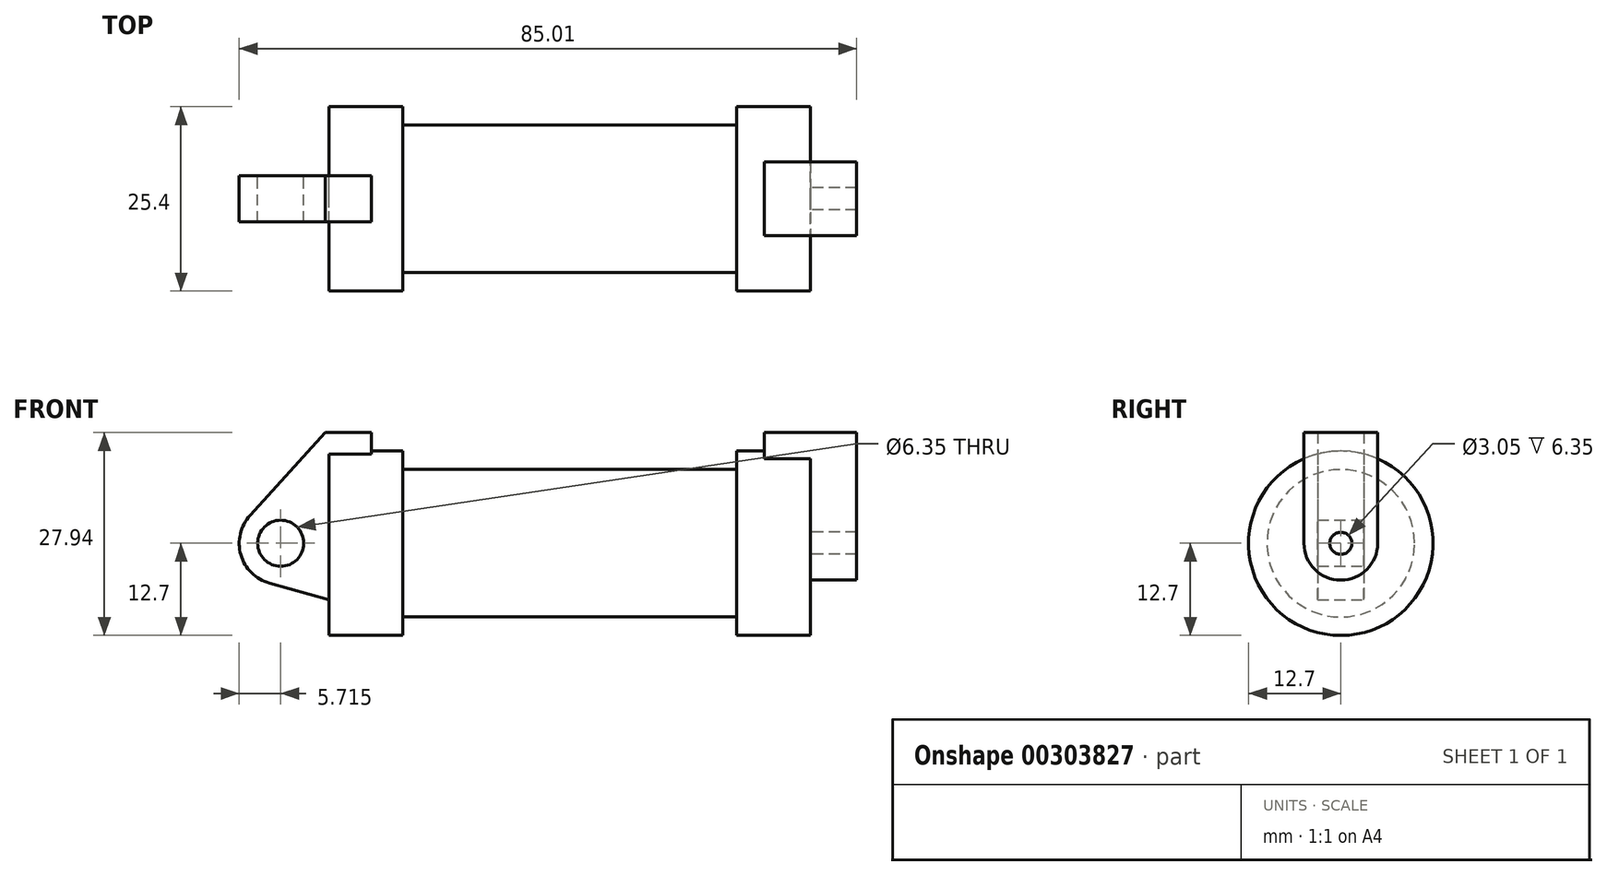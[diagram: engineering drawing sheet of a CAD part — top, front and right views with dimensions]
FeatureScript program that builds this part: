
annotation { "Feature Type Name" : "Feature", "Feature Type Description" : "" }
export const myFeature = defineFeature(function(context is Context, id is Id, definition is map)
    precondition{}
    {
        {
            var Q0;
            Q0=qCreatedBy(makeId("Front.planeOp"),FACE);
            var sketch = newSketch(context, id + "F0", { "sketchPlane" : qUnion([Q0])});
            skLineSegment(sketch, "E0", {"start": v(0, 0) * mm, "end": v(0, 12.7) * mm});
            skLineSegment(sketch, "E1", {"start": v(0, 12.7) * mm, "end": v(10.16, 12.7) * mm});
            skLineSegment(sketch, "E2", {"start": v(10.16, 12.7) * mm, "end": v(10.16, 10.16) * mm});
            skLineSegment(sketch, "E3", {"start": v(10.16, 10.16) * mm, "end": v(56.13, 10.16) * mm});
            skLineSegment(sketch, "E4", {"start": v(56.13, 10.16) * mm, "end": v(56.13, 12.7) * mm});
            skLineSegment(sketch, "E5", {"start": v(56.13, 12.7) * mm, "end": v(66.3, 12.7) * mm});
            skLineSegment(sketch, "E6", {"start": v(66.3, 12.7) * mm, "end": v(66.3, 0) * mm});
            skLineSegment(sketch, "E7", {"start": v(66.3, 0) * mm, "end": v(0, 0) * mm});
            skLineSegment(sketch, "E8", {"start": v(5.84, 15.24) * mm, "end": v(-0.5, 15.24) * mm});
            skLineSegment(sketch, "E9", {"start": v(-0.5, 15.24) * mm, "end": v(-10.88, 3.85) * mm});
            skLineSegment(sketch, "E10", {"start": v(0, 0) * mm, "end": v(-6.65, 0) * mm});
            skCircle(sketch, "E11", {"center": v(-6.65, 0) * mm, "radius": 5.72 * mm});
            skCircle(sketch, "E12", {"center": v(-6.65, 0) * mm, "radius": 3.18 * mm});
            skLineSegment(sketch, "E13", {"start": v(5.84, 15.24) * mm, "end": v(5.84, -9.4) * mm});
            skLineSegment(sketch, "E14", {"start": v(5.84, -9.4) * mm, "end": v(-8.18, -5.5) * mm});
            skSolve(sketch);
        }
        {
            var Q0;
            {var subQ0=sQuery(id+"F0.wireOp",EDGE,"E2");Q0=makeQuery(id+"F0.imprint","IMPRINT",FACE,{"disambiguationData":[TD([[makeQuery(id+"F0.imprint","IMPRINT",EDGE,{"derivedFrom":subQ0}),-1.0]])]});}
            var Q1;
            {var subQ0=sQuery(id+"F0.wireOp",EDGE,"E0");Q1=makeQuery(id+"F0.imprint","IMPRINT",FACE,{"disambiguationData":[TD([[makeQuery(id+"F0.imprint","IMPRINT",EDGE,{"derivedFrom":subQ0}),-1.0]])]});}
            var Q2;
            Q2=sQuery(id+"F0.wireOp",EDGE,"E7");
            revolve(context, id + "F1", {"entities" : qUnion([Q0, Q1]), "axis" : qUnion([Q2]), "revolveType" : RevolveType.FULL});
        }
        {
            var Q0;
            {var subQ1=sQuery(id+"F0.wireOp",EDGE,"E0");Q0=makeQuery(id+"F0.imprint","IMPRINT",FACE,{"disambiguationData":[TD([[makeQuery(id+"F0.imprint","IMPRINT",EDGE,{"derivedFrom":subQ1}),1.0]])]});}
            var Q1;
            {var subQ0=sQuery(id+"F0.wireOp",EDGE,"E0");Q1=makeQuery(id+"F0.imprint","IMPRINT",FACE,{"disambiguationData":[TD([[makeQuery(id+"F0.imprint","IMPRINT",EDGE,{"derivedFrom":subQ0}),-1.0]])]});}
            var Q2;
            {var subQ0=sQuery(id+"F0.wireOp",EDGE,"E14");Q2=makeQuery(id+"F0.imprint","IMPRINT",FACE,{"disambiguationData":[TD([[makeQuery(id+"F0.imprint","IMPRINT",EDGE,{"derivedFrom":subQ0}),-1.0]])]});}
            var Q3;
            Q3=makeQuery(id+"F0.imprint","IMPRINT",FACE,{"disambiguationData":[TD([[makeQuery(id+"F0.imprint","IMPRINT",EDGE,{"derivedFrom":sQuery(id+"F0.wireOp",EDGE,"E12")}),-1.0]])]});
            extrude(context, id + "F2", {"entities" : qUnion([Q0, Q1, Q2, Q3]), "operationType" : NewBodyOperationType.ADD, "endBound" : BoundingType.SYMMETRIC, "depth" : 6.35 * mm});
        }
        {
            var Q0;
            Q0=makeQuery(id+"F1.opRevolve","SWEPT_FACE",FACE,{"disambiguationData":[OSD([sQuery(id+"F0.wireOp",EDGE,"E6")])]});
            var sketch = newSketch(context, id + "F3", { "sketchPlane" : qUnion([Q0])});
            skCircle(sketch, "E15", {"center": v(0, 0) * mm, "radius": 1.52 * mm});
            skCircle(sketch, "E16", {"center": v(0, 0) * mm, "radius": 5.08 * mm});
            skLineSegment(sketch, "E17", {"start": v(-5.08, 0) * mm, "end": v(-5.08, 15.24) * mm});
            skLineSegment(sketch, "E18", {"start": v(-5.08, 15.24) * mm, "end": v(5.08, 15.24) * mm});
            skLineSegment(sketch, "E19", {"start": v(5.08, 15.24) * mm, "end": v(5.08, 0) * mm});
            skSolve(sketch);
        }
        {
            var Q0;
            {var subQ0=sQuery(id+"F3.wireOp",EDGE,"E17");var subQ1=sQuery(id+"F3.wireOp",EDGE,"E16");var subQ2=makeQuery(id+"F3.imprint","INTERSECT",VERTEX,{"derivedFrom":[subQ1,subQ0]});Q0=makeQuery(id+"F3.imprint","IMPRINT",FACE,{"disambiguationData":[TD([[makeQuery(id+"F3.imprint","IMPRINT",EDGE,{"disambiguationData":[TD([[subQ2,1.0]])],"derivedFrom":subQ1}),-1.0]])]});}
            var Q1;
            Q1=makeQuery(id+"F3.imprint","IMPRINT",FACE,{"disambiguationData":[TD([[makeQuery(id+"F3.imprint","IMPRINT",EDGE,{"derivedFrom":sQuery(id+"F3.wireOp",EDGE,"E15")}),-1.0]])]});
            var Q2;
            {var subQ0=sQuery(id+"F3.wireOp",EDGE,"E18");Q2=makeQuery(id+"F3.imprint","IMPRINT",FACE,{"disambiguationData":[TD([[makeQuery(id+"F3.imprint","IMPRINT",EDGE,{"derivedFrom":subQ0}),-1.0]])]});}
            extrude(context, id + "F4", {"entities" : qUnion([Q0, Q1, Q2]), "operationType" : NewBodyOperationType.ADD, "endBound" : BoundingType.SYMMETRIC, "depth" : 12.7 * mm});
        }
    });
